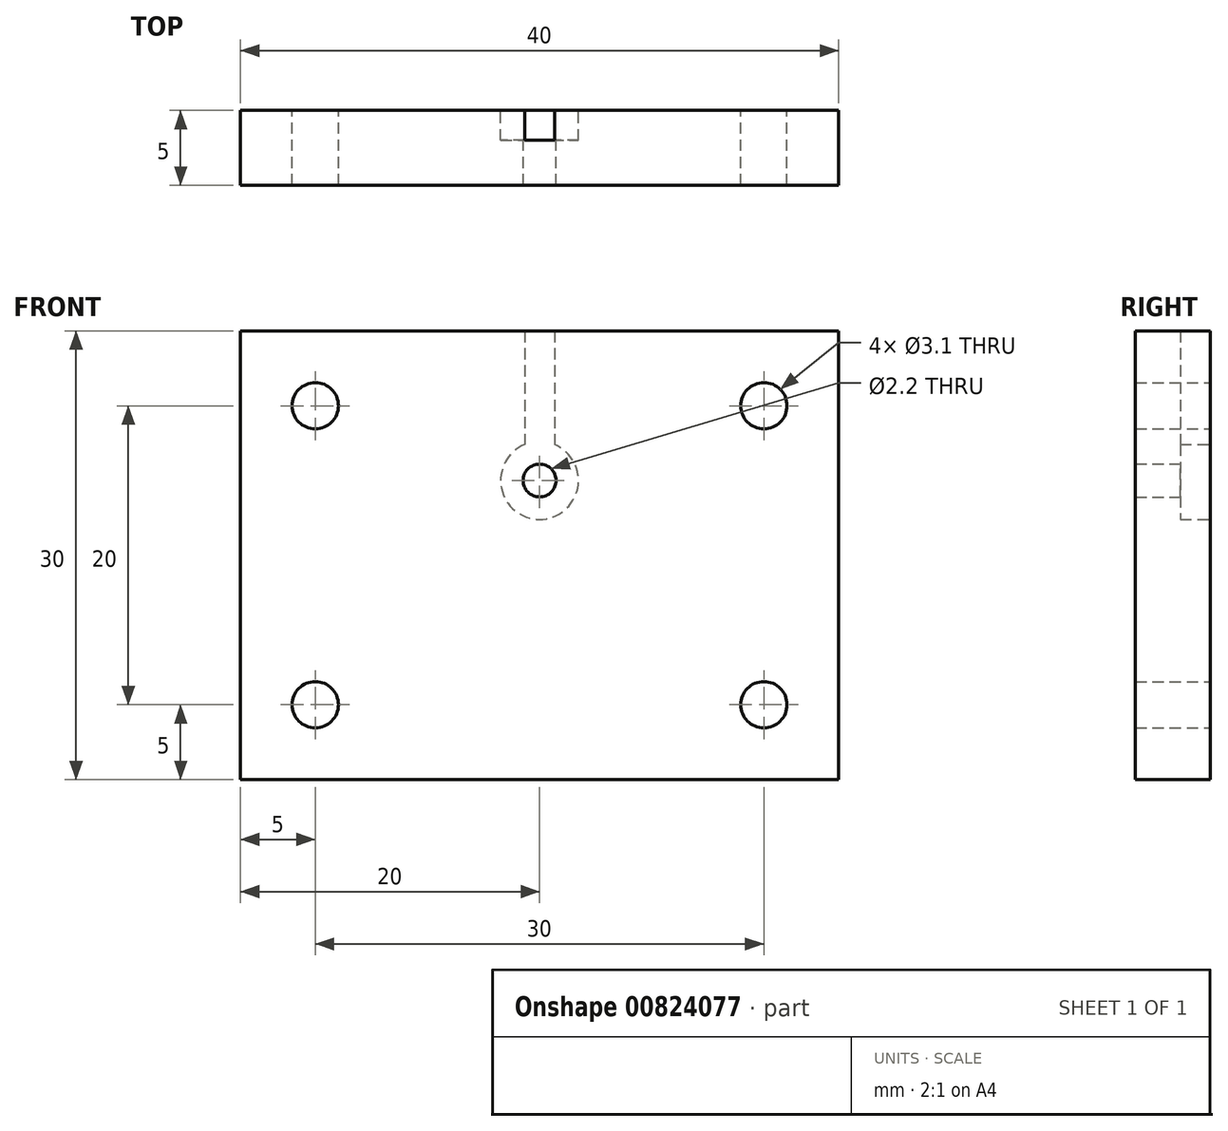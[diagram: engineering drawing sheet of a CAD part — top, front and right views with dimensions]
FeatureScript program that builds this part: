
annotation { "Feature Type Name" : "Feature", "Feature Type Description" : "" }
export const myFeature = defineFeature(function(context is Context, id is Id, definition is map)
    precondition{}
    {
        {
            var Q0;
            Q0=qCreatedBy(makeId("Front.planeOp"),FACE);
            var sketch = newSketch(context, id + "F0", { "sketchPlane" : qUnion([Q0])});
            skLineSegment(sketch, "E0.bottom", {"start": v(20, -15) * mm, "end": v(-20, -15) * mm});
            skLineSegment(sketch, "E0.top", {"start": v(20, 15) * mm, "end": v(-20, 15) * mm});
            skLineSegment(sketch, "E0.left", {"start": v(20, -15) * mm, "end": v(20, 15) * mm});
            skLineSegment(sketch, "E0.right", {"start": v(-20, -15) * mm, "end": v(-20, 15) * mm});
            skPoint(sketch, "E0.middle", {"position": v(0, 0) * mm});
            skArc(sketch, "E1", {"start": v(-1, 7.4) * mm, "mid": v(0, 2.4) * mm, "end": v(1, 7.4) * mm});
            skCircle(sketch, "E2", {"center": v(0, 5) * mm, "radius": 1.1 * mm});
            skLineSegment(sketch, "E3", {"start": v(-1, 15) * mm, "end": v(-1, 7.4) * mm});
            skLineSegment(sketch, "E4.MirrorCS", {"start": v(1, 15) * mm, "end": v(1, 7.4) * mm});
            skCircle(sketch, "E5", {"center": v(15, 10) * mm, "radius": 1.55 * mm});
            skCircle(sketch, "E6.MirrorC", {"center": v(-15, 10) * mm, "radius": 1.55 * mm});
            skCircle(sketch, "E7.MirrorC", {"center": v(15, -10) * mm, "radius": 1.55 * mm});
            skCircle(sketch, "E8.MirrorC", {"center": v(-15, -10) * mm, "radius": 1.55 * mm});
            skSolve(sketch);
        }
        {
            var Q0;
            Q0 = qSketchRegion(id + "F0", true);
            extrude(context, id + "F1", {"entities" : qUnion([Q0]), "depth" : 5 * mm, "offsetDistance" : 25 * mm});
        }
        {
            var Q0;
            Q0=makeQuery(id+"F0.imprint","IMPRINT",FACE,{"disambiguationData":[TD([[makeQuery(id+"F0.imprint","IMPRINT",EDGE,{"derivedFrom":sQuery(id+"F0.wireOp",EDGE,"E1")}),1.0]])]});
            extrude(context, id + "F2", {"entities" : qUnion([Q0]), "operationType" : NewBodyOperationType.REMOVE, "depth" : 2 * mm, "offsetDistance" : 25 * mm});
        }
    });
